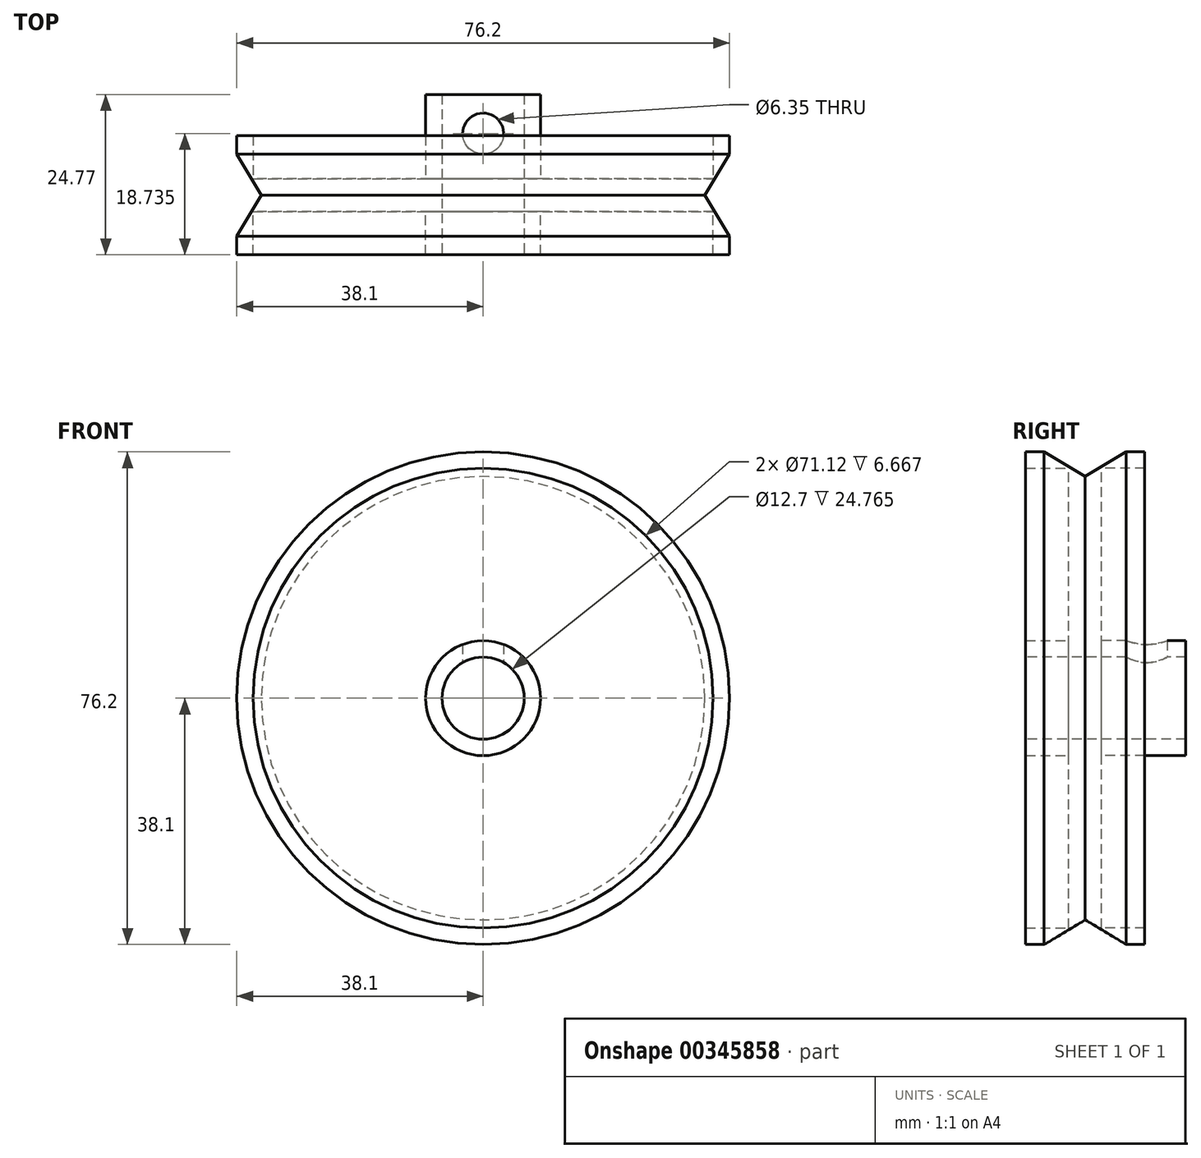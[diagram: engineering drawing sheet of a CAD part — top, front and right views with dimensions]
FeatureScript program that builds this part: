
annotation { "Feature Type Name" : "Feature", "Feature Type Description" : "" }
export const myFeature = defineFeature(function(context is Context, id is Id, definition is map)
    precondition{}
    {
        {
            var Q0;
            Q0=qCreatedBy(makeId("Front.planeOp"),FACE);
            var sketch = newSketch(context, id + "F0", { "sketchPlane" : qUnion([Q0])});
            skCircle(sketch, "E0", {"center": v(0, 0) * mm, "radius": 38.1 * mm});
            skCircle(sketch, "E1", {"center": v(0, 0) * mm, "radius": 6.35 * mm});
            skSolve(sketch);
        }
        {
            var Q0;
            Q0=makeQuery(id+"F0.imprint","IMPRINT",FACE,{"disambiguationData":[TD([[makeQuery(id+"F0.imprint","IMPRINT",EDGE,{"derivedFrom":sQuery(id+"F0.wireOp",EDGE,"E0")}),1.0]])]});
            extrude(context, id + "F2", {"entities" : qUnion([Q0]), "oppositeDirection" : true, "depth" : 9.2 * mm});
        }
        {
            var Q0;
            Q0=makeQuery(id+"F2.opExtrude","CAP_FACE",FACE,{"disambiguationData":[OSD([sQuery(id+"F0.wireOp",EDGE,"E0"),sQuery(id+"F0.wireOp",EDGE,"E1")])],"isStart":false});
            shell(context, id + "F3", {"entities" : qUnion([Q0]), "thickness" : 2.54 * mm});
        }
        {
            var Q0;
            Q0=makeQuery(id+"F2.opExtrude","CAP_EDGE",EDGE,{"disambiguationData":[OSD([sQuery(id+"F0.wireOp",EDGE,"E0")])],"isStart":true});
            chamfer(context, id + "F4", {"entities" : qUnion([Q0]), "chamferType" : ChamferType.TWO_OFFSETS, "width1" : 3.8 * mm, "oppositeDirection" : false, "width2" : 6.35 * mm, "tangentPropagation" : true});
        }
        {
            var Q0;
            Q0=makeQuery(id+"F2.opExtrude","SWEPT_BODY",BODY,{"disambiguationData":[OSD([sQuery(id+"F0.wireOp",EDGE,"E0"),sQuery(id+"F0.wireOp",EDGE,"E1")])]});
            var Q1;
            Q1=qCreatedBy(makeId("Front.planeOp"),FACE);
            mirror(context, id + "F1", {"operationType" : NewBodyOperationType.ADD, "entities" : qUnion([Q0]), "mirrorPlane" : qUnion([Q1])});
        }
        {
            var Q0;
            {var subQ0=sQuery(id+"F0.wireOp",EDGE,"E1");var subQ1=sQuery(id+"F0.wireOp",EDGE,"E0");Q0=makeQuery(id+"F3.opShell","OFFSET_FACE",FACE,{"disambiguationData":[OSD([subQ1,subQ0]),TDD([makeQuery(id+"F2.opExtrude","CAP_FACE",FACE,{"disambiguationData":[OSD([subQ1,subQ0])],"isStart":false})])]});}
            extrude(context, id + "F5", {"entities" : qUnion([Q0]), "operationType" : NewBodyOperationType.ADD, "depth" : 6.35 * mm});
        }
        {
            var Q0;
            Q0=qCreatedBy(makeId("Top.planeOp"),FACE);
            var sketch = newSketch(context, id + "F6", { "sketchPlane" : qUnion([Q0])});
            skPoint(sketch, "E2", {"position": v(0, 9.53) * mm});
            skSolve(sketch);
        }
        {
            var Q0;
            Q0=sQuery(id+"F6.wireOp",VERTEX,"E2");
            var Q1;
            Q1=makeQuery(id+"F2.opExtrude","SWEPT_BODY",BODY,{"disambiguationData":[OSD([sQuery(id+"F0.wireOp",EDGE,"E0"),sQuery(id+"F0.wireOp",EDGE,"E1")])]});
            hole(context, id + "F7", {"style" : HoleStyle.SIMPLE, "endStyle" : HoleEndStyle.BLIND, "oppositeDirection" : true, "holeDiameter" : 6.35 * mm, "holeDepth" : 12.7 * mm, "locations" : qUnion([Q0]), "scope" : qUnion([Q1])});
        }
    });
